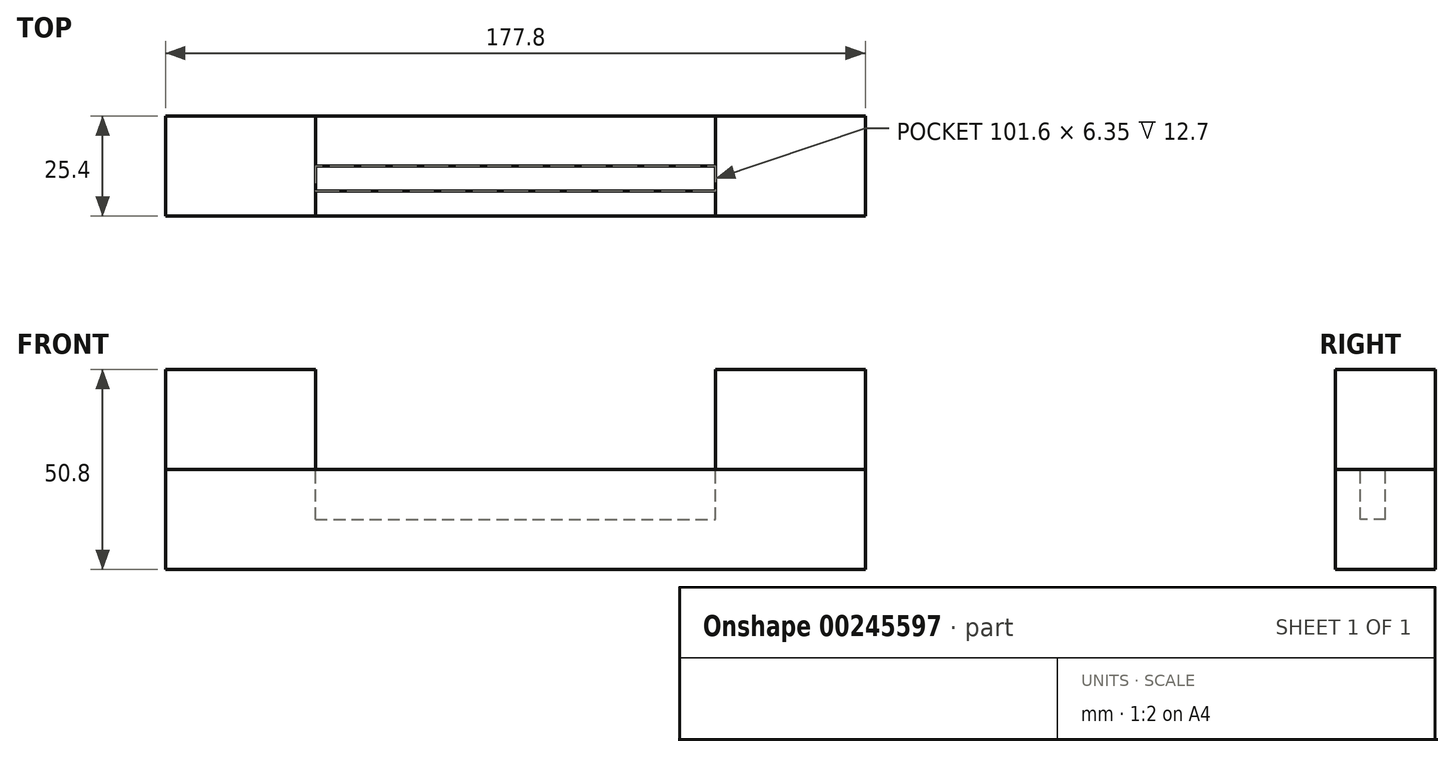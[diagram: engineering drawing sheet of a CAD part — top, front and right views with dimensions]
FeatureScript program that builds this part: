
annotation { "Feature Type Name" : "Feature", "Feature Type Description" : "" }
export const myFeature = defineFeature(function(context is Context, id is Id, definition is map)
    precondition{}
    {
        {
            var Q0;
            Q0=qCreatedBy(makeId("Top.planeOp"),FACE);
            var sketch = newSketch(context, id + "F0", { "sketchPlane" : qUnion([Q0])});
            skLineSegment(sketch, "E0.bottom", {"start": v(-88.9, 12.7) * mm, "end": v(88.9, 12.7) * mm});
            skLineSegment(sketch, "E0.top", {"start": v(-88.9, -12.7) * mm, "end": v(88.9, -12.7) * mm});
            skLineSegment(sketch, "E0.left", {"start": v(-88.9, 12.7) * mm, "end": v(-88.9, -12.7) * mm});
            skLineSegment(sketch, "E0.right", {"start": v(88.9, 12.7) * mm, "end": v(88.9, -12.7) * mm});
            skPoint(sketch, "E0.middle", {"position": v(0, 0) * mm});
            skSolve(sketch);
        }
        {
            var Q0;
            Q0=makeQuery(id+"F0.imprint","IMPRINT",FACE,{"disambiguationData":[TD([[makeQuery(id+"F0.imprint","IMPRINT",EDGE,{"derivedFrom":sQuery(id+"F0.wireOp",EDGE,"E0.bottom")}),-1.0]])]});
            extrude(context, id + "F1", {"entities" : qUnion([Q0]), "depth" : 25.4 * mm});
        }
        {
            var Q0;
            Q0=makeQuery(id+"F1.opExtrude","CAP_FACE",FACE,{"disambiguationData":[OSD([sQuery(id+"F0.wireOp",EDGE,"E0.bottom"),sQuery(id+"F0.wireOp",EDGE,"E0.top"),sQuery(id+"F0.wireOp",EDGE,"E0.left"),sQuery(id+"F0.wireOp",EDGE,"E0.right")])],"isStart":false});
            var sketch = newSketch(context, id + "F2", { "sketchPlane" : qUnion([Q0])});
            skLineSegment(sketch, "E1.bottom", {"start": v(-88.9, 12.7) * mm, "end": v(-50.8, 12.7) * mm});
            skLineSegment(sketch, "E1.top", {"start": v(-88.9, -12.7) * mm, "end": v(-50.8, -12.7) * mm});
            skLineSegment(sketch, "E1.left", {"start": v(-88.9, 12.7) * mm, "end": v(-88.9, -12.7) * mm});
            skLineSegment(sketch, "E1.right", {"start": v(-50.8, 12.7) * mm, "end": v(-50.8, -12.7) * mm});
            skPoint(sketch, "E1.middle", {"position": v(-69.85, 0) * mm});
            skSolve(sketch);
        }
        {
            var Q0;
            Q0 = qSketchRegion(id + "F2", true);
            extrude(context, id + "F3", {"entities" : qUnion([Q0]), "depth" : 25.4 * mm});
        }
        {
            var Q0;
            Q0=makeQuery(id+"F3.opExtrude","SWEPT_BODY",BODY,{"disambiguationData":[OSD([sQuery(id+"F2.wireOp",EDGE,"E1.bottom"),sQuery(id+"F2.wireOp",EDGE,"E1.top"),sQuery(id+"F2.wireOp",EDGE,"E1.left"),sQuery(id+"F2.wireOp",EDGE,"E1.right")])]});
            var Q1;
            Q1=qCreatedBy(makeId("Right.planeOp"),FACE);
            mirror(context, id + "F4", {"entities" : qUnion([Q0]), "mirrorPlane" : qUnion([Q1])});
        }
        {
            var Q0;
            Q0=makeQuery(id+"F1.opExtrude","CAP_FACE",FACE,{"disambiguationData":[OSD([sQuery(id+"F0.wireOp",EDGE,"E0.bottom"),sQuery(id+"F0.wireOp",EDGE,"E0.top"),sQuery(id+"F0.wireOp",EDGE,"E0.left"),sQuery(id+"F0.wireOp",EDGE,"E0.right")])],"isStart":false});
            var sketch = newSketch(context, id + "F5", { "sketchPlane" : qUnion([Q0])});
            skLineSegment(sketch, "E2.0", {"start": v(-50.8, 12.7) * mm, "end": v(-50.8, -12.7) * mm, "construction": true});
            skLineSegment(sketch, "E3.0", {"start": v(50.8, 12.7) * mm, "end": v(50.8, -12.7) * mm, "construction": true});
            skLineSegment(sketch, "E4.bottom", {"start": v(-50.8, 0) * mm, "end": v(50.8, 0) * mm});
            skLineSegment(sketch, "E4.top", {"start": v(-50.8, -6.35) * mm, "end": v(50.8, -6.35) * mm});
            skLineSegment(sketch, "E4.left", {"start": v(-50.8, 0) * mm, "end": v(-50.8, -6.35) * mm});
            skLineSegment(sketch, "E4.right", {"start": v(50.8, 0) * mm, "end": v(50.8, -6.35) * mm});
            skSolve(sketch);
        }
        {
            var Q0;
            Q0=makeQuery(id+"F5.imprint","IMPRINT",FACE,{"disambiguationData":[TD([[makeQuery(id+"F5.imprint","IMPRINT",EDGE,{"derivedFrom":sQuery(id+"F5.wireOp",EDGE,"E4.bottom")}),-1.0]])]});
            extrude(context, id + "F6", {"entities" : qUnion([Q0]), "operationType" : NewBodyOperationType.REMOVE, "oppositeDirection" : true, "depth" : 12.7 * mm});
        }
    });
